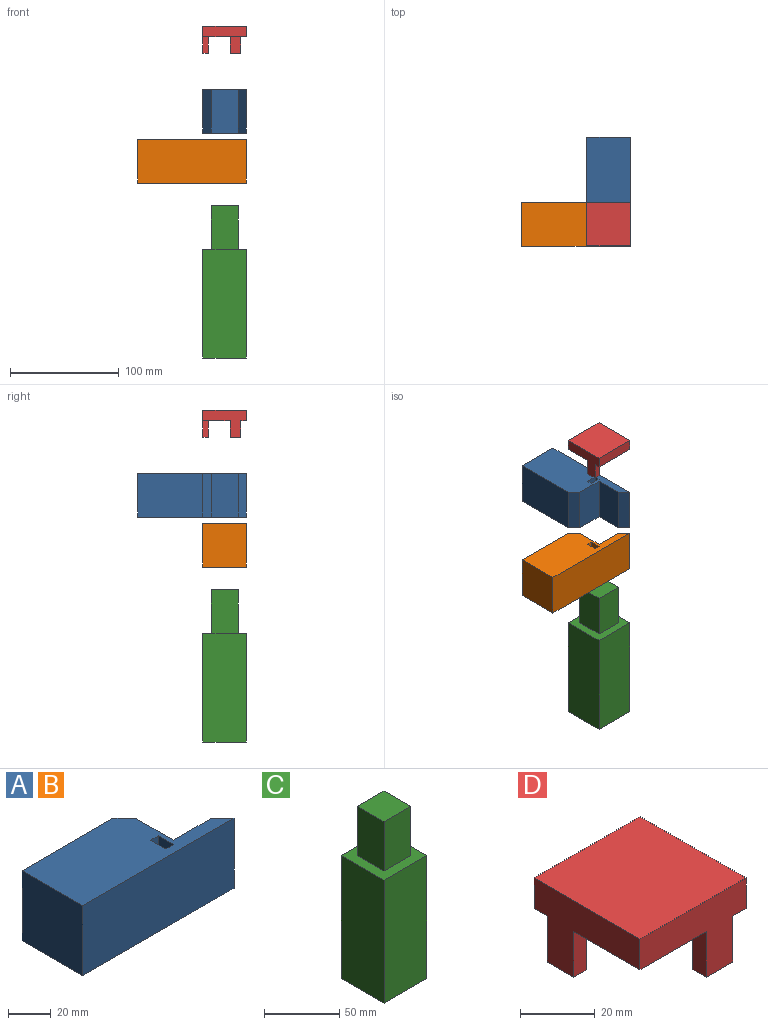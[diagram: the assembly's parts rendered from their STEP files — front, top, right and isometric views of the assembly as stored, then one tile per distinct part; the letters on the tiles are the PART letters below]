
ASSEMBLY  parts=4 mates=7
PART A: 13 faces, bbox 100x40x40 mm
  f0: plane 100x40mm, normal (0,0,-1), area 2837.5mm2, adj f2,f3,f4,f5,f6,f7,f8,f9
  f1: plane 100x40mm, normal (0,0,1), area 2837.5mm2, adj f2,f3,f4,f5,f6,f7,f8,f9
  f2: plane 40x7.5mm, normal (0.71,0.71,0), area 424.3mm2, adj f0,f1,f4,f7
  f3: plane 60x40mm, normal (0,1,0), area 2400mm2, adj f0,f1,f5,f6
  f4: plane 100x40mm, normal (0,-1,0), area 4000mm2, adj f0,f1,f2,f5
  f5: plane 40x40mm, normal (-1,0,0), area 1600mm2, adj f0,f1,f3,f4
  f6: plane 40x7.5mm, normal (0.71,0.71,0), area 424.3mm2, adj f0,f1,f3,f8
  f7: plane 40x25mm, normal (0,1,0), area 1000mm2, adj f0,f1,f2,f8
  f8: plane 40x25mm, normal (1,0,0), area 1000mm2, adj f0,f1,f6,f7
  f9: plane 40x10mm, normal (1,0,0), area 400mm2, adj f0,f1,f10,f12
  f10: plane 40x5mm, normal (0,1,0), area 200mm2, adj f0,f1,f9,f11
  f11: plane 40x10mm, normal (-1,0,0), area 400mm2, adj f0,f1,f10,f12
  f12: plane 40x5mm, normal (0,-1,0), area 200mm2, adj f0,f1,f9,f11
PART B: same geometry as A
PART C: 11 faces, bbox 40x40x140 mm
  f0: plane 40x40mm, normal (0,0,1), area 975mm2, adj f1,f2,f3,f4,f6,f7,f8,f9
  f1: plane 100x40mm, normal (0,-1,0), area 4000mm2, adj f0,f2,f4,f5
  f2: plane 100x40mm, normal (1,0,0), area 4000mm2, adj f0,f1,f3,f5
  f3: plane 100x40mm, normal (0,1,0), area 4000mm2, adj f0,f2,f4,f5
  f4: plane 100x40mm, normal (-1,0,0), area 4000mm2, adj f0,f1,f3,f5
  f5: plane 40x40mm, normal (0,0,-1), area 1600mm2, adj f1,f2,f3,f4
  f6: plane 40x25mm, normal (0,-1,0), area 1000mm2, adj f0,f7,f9,f10
  f7: plane 40x25mm, normal (1,0,0), area 1000mm2, adj f0,f6,f8,f10
  f8: plane 40x25mm, normal (0,1,0), area 1000mm2, adj f0,f7,f9,f10
  f9: plane 40x25mm, normal (-1,0,0), area 1000mm2, adj f0,f6,f8,f10
  f10: plane 25x25mm, normal (0,0,1), area 625mm2, adj f6,f7,f8,f9
PART D: 14 faces, bbox 40x40x25 mm
  f0: plane 40x25mm, normal (0,-1,0), area 550mm2, adj f1,f3,f4,f5,f11,f12,f13
  f1: plane 40x10mm, normal (1,0,0), area 400mm2, adj f0,f2,f4,f5
  f2: plane 40x10mm, normal (0,1,0), area 400mm2, adj f1,f3,f4,f5
  f3: plane 40x25mm, normal (-1,0,0), area 550mm2, adj f0,f2,f4,f5,f6,f8,f9
  f4: plane 40x40mm, normal (0,0,1), area 1600mm2, adj f0,f1,f2,f3
  f5: plane 40x40mm, normal (0,0,-1), area 1500mm2, adj f0,f1,f2,f3,f6,f7,f8,f10
  f6: plane 15x5mm, normal (0,1,0), area 75mm2, adj f3,f5,f7,f9
  f7: plane 15x10mm, normal (1,0,0), area 150mm2, adj f5,f6,f8,f9
  f8: plane 15x5mm, normal (0,-1,0), area 75mm2, adj f3,f5,f7,f9
  f9: plane 10x5mm, normal (0,0,-1), area 50mm2, adj f3,f6,f7,f8
  f10: plane 15x10mm, normal (0,1,0), area 150mm2, adj f5,f11,f12,f13
  f11: plane 15x5mm, normal (1,0,0), area 75mm2, adj f0,f5,f10,f13
  f12: plane 15x5mm, normal (-1,0,0), area 75mm2, adj f0,f5,f10,f13
  f13: plane 10x5mm, normal (0,0,-1), area 50mm2, adj f0,f10,f11,f12
PLACE A rot(axis=(0.71,-0.71,0),180deg) t=(-56.98,86.62,211.27)mm
PLACE B t=(-136.98,6.62,165.27)mm
PLACE C t=(-56.98,6.62,-15.73)mm fixed
PLACE D rot(axis=(0,0,-1),90deg) t=(-56.98,6.62,279.77)mm
MATE planar D.f0 <-> B.f9  axis (-1,0,0) through (-76.98,-8.38,272.27)mm
MATE planar A.f7 <-> C.f7  axis (-1,0,0) through (-44.48,6.62,211.27)mm
MATE planar B.f8 <-> C.f9  axis (1,0,0) through (-69.48,6.62,165.27)mm
MATE planar B.f7 <-> C.f6  axis (0,1,0) through (-56.98,-5.88,165.27)mm
MATE planar A.f8 <-> C.f8  axis (0,-1,0) through (-56.98,19.12,211.27)mm
MATE planar D.f11 <-> B.f10  axis (0,-1,0) through (-74.48,-8.38,272.27)mm
MATE planar B.f4 <-> B.f4  axis (0,-1,0) through (-86.98,-13.38,165.27)mm
